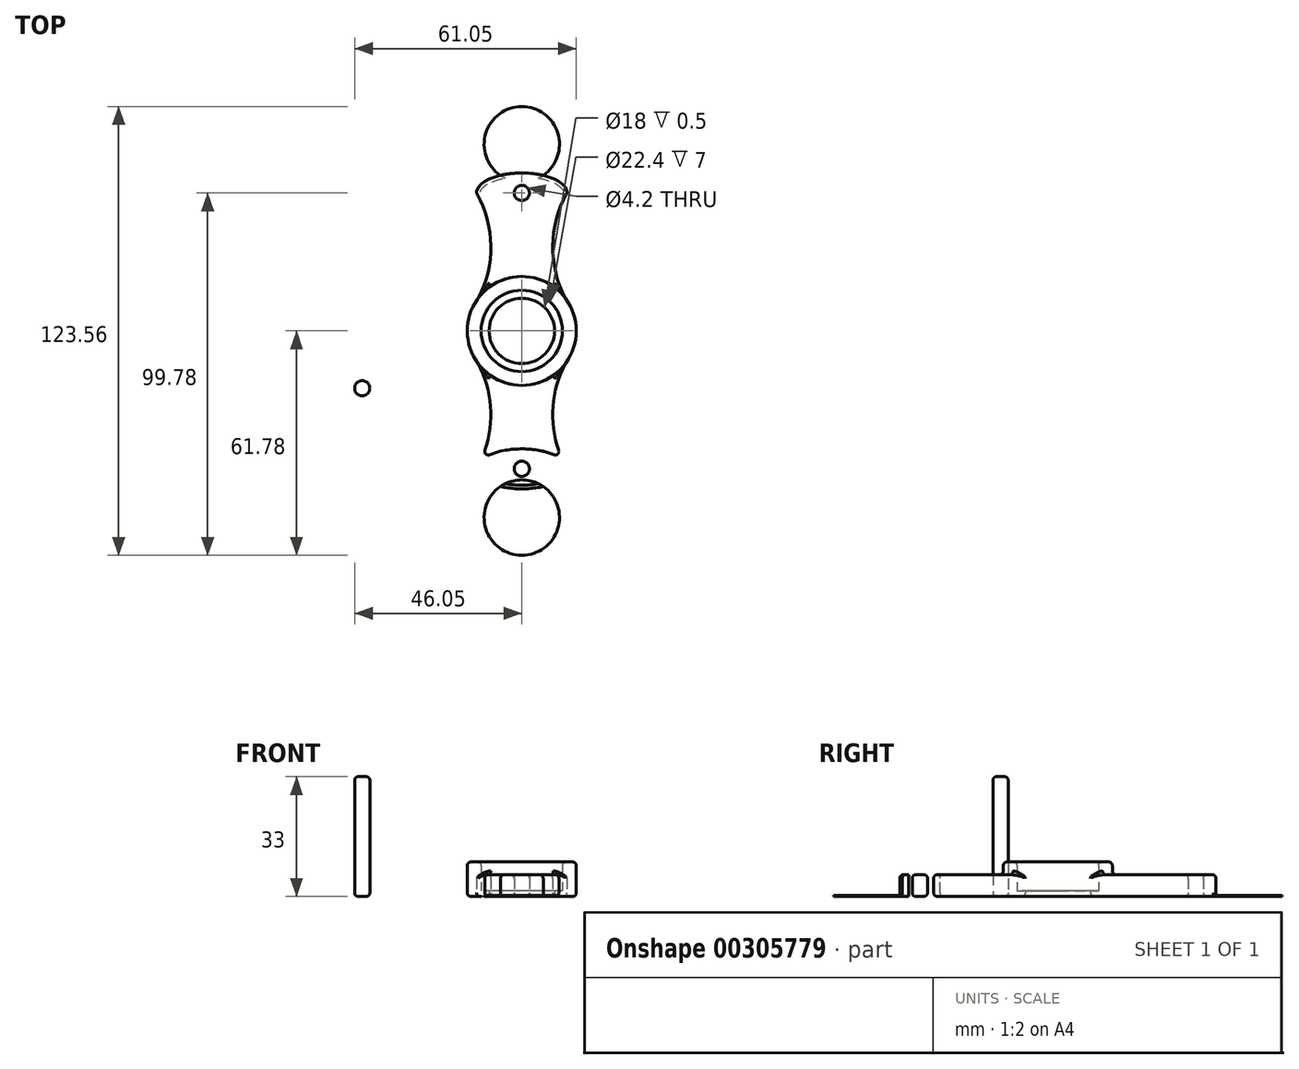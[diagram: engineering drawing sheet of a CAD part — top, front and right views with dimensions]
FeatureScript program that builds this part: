
annotation { "Feature Type Name" : "Feature", "Feature Type Description" : "" }
export const myFeature = defineFeature(function(context is Context, id is Id, definition is map)
    precondition{}
    {
        {
            var Q0;
            Q0=qCreatedBy(makeId("Top.planeOp"),FACE);
            var sketch = newSketch(context, id + "F0", { "sketchPlane" : qUnion([Q0])});
            skCircle(sketch, "E0", {"center": v(0, 38) * mm, "radius": 2.1 * mm});
            skCircle(sketch, "E1", {"center": v(0, 0) * mm, "radius": 9 * mm});
            skCircle(sketch, "E2", {"center": v(0, 0) * mm, "radius": 11.2 * mm});
            skCircle(sketch, "E3", {"center": v(0, 0) * mm, "radius": 15 * mm});
            skArc(sketch, "E4.MirrorCS", {"start": v(-12, -9) * mm, "mid": v(-11.4, -10.22) * mm, "end": v(-10.83, -11.46) * mm});
            skCircle(sketch, "E5.MirrorC", {"center": v(0, -38) * mm, "radius": 2.1 * mm});
            skEllipse(sketch, "E6", {"center": v(0, -38) * mm, "majorRadius": 5.5 * mm, "minorRadius": 12.5 * mm, "majorAxis": v(0, -1)});
            skArc(sketch, "E7", {"start": v(-12.5, -38) * mm, "mid": v(-8.51, -23.56) * mm, "end": v(-12, -9) * mm});
            skPoint(sketch, "E8.MirrorCS.start.orphan", {"position": v(12, -9) * mm});
            skArc(sketch, "E9.MirrorCS", {"start": v(12.5, -38) * mm, "mid": v(8.51, -23.56) * mm, "end": v(12, -9) * mm});
            skPoint(sketch, "E10.orphan", {"position": v(-12.5, -38) * mm});
            skPoint(sketch, "E11.orphan", {"position": v(12.5, -38) * mm});
            skArc(sketch, "E12.MirrorCS", {"start": v(-12.5, 38) * mm, "mid": v(-8.51, 23.56) * mm, "end": v(-12, 9) * mm});
            skArc(sketch, "E13.MirrorCS", {"start": v(12.5, 38) * mm, "mid": v(8.51, 23.56) * mm, "end": v(12, 9) * mm});
            skEllipse(sketch, "E14.MirrorC", {"center": v(0, 38) * mm, "majorRadius": 5.5 * mm, "minorRadius": 12.5 * mm, "majorAxis": v(0, 1)});
            skCircle(sketch, "E15.MirrorC", {"center": v(-31.5, -36.18) * mm, "radius": 2.1 * mm});
            skEllipse(sketch, "E16", {"center": v(-31.5, -36.18) * mm, "majorRadius": 5.5 * mm, "minorRadius": 12.5 * mm, "majorAxis": v(0, -1)});
            skCircle(sketch, "E17.MirrorC", {"center": v(-43.95, -15.8) * mm, "radius": 2.1 * mm});
            skEllipticalArc(sketch, "E18", {});
            skCircle(sketch, "E19", {"center": v(0, -51.4) * mm, "radius": 10.38 * mm});
            skCircle(sketch, "E20.MirrorC", {"center": v(0, 51.4) * mm, "radius": 10.38 * mm});
            skArc(sketch, "E21", {"start": v(-55.22, -13.41) * mm, "mid": v(-53.63, -9.12) * mm, "end": v(-52.7, -4.64) * mm});
            skArc(sketch, "E22.MirrorCS", {"start": v(-32.68, -13.41) * mm, "mid": v(-34.28, -9.12) * mm, "end": v(-35.2, -4.64) * mm});
            skPoint(sketch, "E23.orphan", {"position": v(-56.45, -15.8) * mm});
            skArc(sketch, "E24", {"start": v(-39.27, -0.36) * mm, "mid": v(-43.95, 0.06) * mm, "end": v(-48.64, -0.36) * mm});
            skPoint(sketch, "E25.visualSharp", {"position": v(-52.47, -1.36) * mm});
            skArc(sketch, "E25.filletArc", {"start": v(-48.64, -0.36) * mm, "mid": v(-51.37, -1.83) * mm, "end": v(-52.7, -4.64) * mm});
            skPoint(sketch, "E26.visualSharp", {"position": v(-35.44, -1.36) * mm});
            skArc(sketch, "E26.filletArc", {"start": v(-35.2, -4.64) * mm, "mid": v(-36.54, -1.83) * mm, "end": v(-39.27, -0.36) * mm});
            const initialGuessF0  = {"E18": [-0.04395357987462184, -0.015792207916784852, 0, -1, 0.0055, 0.0125, 4.265086725092129, 2.0180985820874437]};
            skSetInitialGuess(sketch, initialGuessF0);
            skSolve(sketch);
        }
        {
            var Q0;
            Q0=makeQuery(id+"F0.imprint","IMPRINT",FACE,{"disambiguationData":[TD([[makeQuery(id+"F0.imprint","IMPRINT",EDGE,{"derivedFrom":sQuery(id+"F0.wireOp",EDGE,"E1")}),-1.0]])]});
            extrude(context, id + "F1", {"entities" : qUnion([Q0]), "depth" : 1.5 * mm});
        }
        {
            var Q0;
            Q0=makeQuery(id+"F0.imprint","IMPRINT",FACE,{"disambiguationData":[TD([[makeQuery(id+"F0.imprint","IMPRINT",EDGE,{"derivedFrom":sQuery(id+"F0.wireOp",EDGE,"E2")}),-1.0]])]});
            extrude(context, id + "F2", {"entities" : qUnion([Q0]), "operationType" : NewBodyOperationType.ADD, "depth" : 9.5 * mm});
        }
        {
            var Q0;
            {var subQ0=sQuery(id+"F0.wireOp",EDGE,"E12.MirrorCS");var subQ1=sQuery(id+"F0.wireOp",EDGE,"E3");var subQ2=makeQuery(id+"F0.imprint","INTERSECT",VERTEX,{"derivedFrom":[subQ1,subQ0]});Q0=makeQuery(id+"F0.imprint","IMPRINT",FACE,{"disambiguationData":[TD([[makeQuery(id+"F0.imprint","IMPRINT",EDGE,{"disambiguationData":[TD([[subQ2,1.0]])],"derivedFrom":subQ1}),-1.0]])]});}
            var Q1;
            Q1=makeQuery(id+"F0.imprint","IMPRINT",FACE,{"disambiguationData":[TD([[makeQuery(id+"F0.imprint","IMPRINT",EDGE,{"derivedFrom":sQuery(id+"F0.wireOp",EDGE,"E0")}),-1.0]])]});
            var Q2;
            {var subQ3=sQuery(id+"F0.wireOp",EDGE,"E6");var subQ7=sQuery(id+"F0.wireOp",EDGE,"E9.MirrorCS");var subQ8=makeQuery(id+"F0.imprint","INTERSECT",VERTEX,{"disambiguationData":[OD(1.0)],"derivedFrom":[subQ3,subQ7]});Q2=makeQuery(id+"F0.imprint","IMPRINT",FACE,{"disambiguationData":[TD([[makeQuery(id+"F0.imprint","IMPRINT",EDGE,{"disambiguationData":[TD([[subQ8,-1.0]])],"derivedFrom":subQ3}),-1.0]])]});}
            var Q3;
            Q3=makeQuery(id+"F0.imprint","IMPRINT",FACE,{"disambiguationData":[TD([[makeQuery(id+"F0.imprint","IMPRINT",EDGE,{"derivedFrom":sQuery(id+"F0.wireOp",EDGE,"E5.MirrorC")}),1.0]])]});
            var Q4;
            {var subQ0=sQuery(id+"F0.wireOp",EDGE,"E20.MirrorC");var subQ1=sQuery(id+"F0.wireOp",EDGE,"E14.MirrorC");var subQ2=makeQuery(id+"F0.imprint","INTERSECT",VERTEX,{"disambiguationData":[OD(0.0)],"derivedFrom":[subQ1,subQ0]});Q4=makeQuery(id+"F0.imprint","IMPRINT",FACE,{"disambiguationData":[TD([[makeQuery(id+"F0.imprint","IMPRINT",EDGE,{"disambiguationData":[TD([[subQ2,-1.0]])],"derivedFrom":subQ1}),1.0]])]});}
            var Q5;
            {var subQ0=sQuery(id+"F0.wireOp",EDGE,"E19");var subQ1=sQuery(id+"F0.wireOp",EDGE,"E6");var subQ2=makeQuery(id+"F0.imprint","INTERSECT",VERTEX,{"disambiguationData":[OD(0.0)],"derivedFrom":[subQ1,subQ0]});Q5=makeQuery(id+"F0.imprint","IMPRINT",FACE,{"disambiguationData":[TD([[makeQuery(id+"F0.imprint","IMPRINT",EDGE,{"disambiguationData":[TD([[subQ2,-1.0]])],"derivedFrom":subQ1}),1.0]])]});}
            extrude(context, id + "F3", {"entities" : qUnion([Q0, Q1, Q2, Q3, Q4, Q5]), "operationType" : NewBodyOperationType.ADD, "depth" : 6 * mm});
        }
        {
            var Q0;
            Q0=makeQuery(id+"F0.imprint","IMPRINT",FACE,{"disambiguationData":[TD([[makeQuery(id+"F0.imprint","IMPRINT",EDGE,{"derivedFrom":sQuery(id+"F0.wireOp",EDGE,"E17.MirrorC")}),1.0]])]});
            var Q1;
            Q1=makeQuery(id+"F0.imprint","IMPRINT",FACE,{"disambiguationData":[TD([[makeQuery(id+"F0.imprint","IMPRINT",EDGE,{"derivedFrom":sQuery(id+"F0.wireOp",EDGE,"E15.MirrorC")}),1.0]])]});
            extrude(context, id + "F4", {"entities" : qUnion([Q0, Q1]), "depth" : 33 * mm});
        }
        {
            var Q0;
            Q0=makeQuery(id+"F4.opExtrude","CAP_FACE",FACE,{"disambiguationData":[OSD([sQuery(id+"F0.wireOp",EDGE,"E17.MirrorC"),sQuery(id+"F0.wireOp",EDGE,"E18")])],"isStart":true});
            var Q1;
            Q1=makeQuery(id+"F4.opExtrude","CAP_EDGE",EDGE,{"disambiguationData":[OSD([sQuery(id+"F0.wireOp",EDGE,"E18")])],"isStart":false});
            var Q2;
            Q2=makeQuery(id+"F4.opExtrude","CAP_FACE",FACE,{"disambiguationData":[OSD([sQuery(id+"F0.wireOp",EDGE,"E17.MirrorC"),sQuery(id+"F0.wireOp",EDGE,"E18")])],"isStart":false});
            var Q3;
            Q3=makeQuery(id+"F4.opExtrude","SWEPT_FACE",FACE,{"disambiguationData":[OSD([sQuery(id+"F0.wireOp",EDGE,"E18")])]});
            var Q4;
            Q4=makeQuery(id+"F4.opExtrude","SWEPT_FACE",FACE,{"disambiguationData":[OSD([sQuery(id+"F0.wireOp",EDGE,"E17.MirrorC")])]});
            var Q5;
            Q5=makeQuery(id+"F4.opExtrude","SWEPT_FACE",FACE,{"disambiguationData":[OSD([sQuery(id+"F0.wireOp",EDGE,"E16")])]});
            var Q6;
            Q6=makeQuery(id+"F4.opExtrude","CAP_EDGE",EDGE,{"disambiguationData":[OSD([sQuery(id+"F0.wireOp",EDGE,"E16")])],"isStart":false});
            var Q7;
            Q7=makeQuery(id+"F4.opExtrude","CAP_FACE",FACE,{"disambiguationData":[OSD([sQuery(id+"F0.wireOp",EDGE,"E15.MirrorC"),sQuery(id+"F0.wireOp",EDGE,"E16")])],"isStart":false});
            var Q8;
            Q8=makeQuery(id+"F4.opExtrude","CAP_FACE",FACE,{"disambiguationData":[OSD([sQuery(id+"F0.wireOp",EDGE,"E15.MirrorC"),sQuery(id+"F0.wireOp",EDGE,"E16")])],"isStart":true});
            var Q9;
            Q9=makeQuery(id+"F4.opExtrude","SWEPT_FACE",FACE,{"disambiguationData":[OSD([sQuery(id+"F0.wireOp",EDGE,"E15.MirrorC")])]});
            var Q10;
            Q10=makeQuery(id+"F4.opExtrude","CAP_EDGE",EDGE,{"disambiguationData":[OSD([sQuery(id+"F0.wireOp",EDGE,"E18")])],"isStart":true});
            var Q11;
            Q11=makeQuery(id+"F4.opExtrude","CAP_EDGE",EDGE,{"disambiguationData":[OSD([sQuery(id+"F0.wireOp",EDGE,"E17.MirrorC")])],"isStart":false});
            var Q12;
            Q12=makeQuery(id+"F4.opExtrude","CAP_EDGE",EDGE,{"disambiguationData":[OSD([sQuery(id+"F0.wireOp",EDGE,"E17.MirrorC")])],"isStart":true});
            var Q13;
            Q13=makeQuery(id+"F4.opExtrude","CAP_EDGE",EDGE,{"disambiguationData":[OSD([sQuery(id+"F0.wireOp",EDGE,"E16")])],"isStart":true});
            var Q14;
            Q14=makeQuery(id+"F4.opExtrude","CAP_EDGE",EDGE,{"disambiguationData":[OSD([sQuery(id+"F0.wireOp",EDGE,"E15.MirrorC")])],"isStart":false});
            var Q15;
            Q15=makeQuery(id+"F4.opExtrude","CAP_EDGE",EDGE,{"disambiguationData":[OSD([sQuery(id+"F0.wireOp",EDGE,"E15.MirrorC")])],"isStart":true});
            fillet(context, id + "F5", {"entities" : qUnion([Q0, Q1, Q2, Q3, Q4, Q5, Q6, Q7, Q8, Q9, Q10, Q11, Q12, Q13, Q14, Q15]), "radius" : 1 * mm, "tangentPropagation" : true, "allowEdgeOverflow" : false});
        }
        {
            var Q0;
            {var subQ0=sQuery(id+"F0.wireOp",EDGE,"E19");var subQ1=sQuery(id+"F0.wireOp",EDGE,"E6");var subQ2=makeQuery(id+"F0.imprint","INTERSECT",VERTEX,{"disambiguationData":[OD(0.0)],"derivedFrom":[subQ1,subQ0]});Q0=makeQuery(id+"F0.imprint","IMPRINT",FACE,{"disambiguationData":[TD([[makeQuery(id+"F0.imprint","IMPRINT",EDGE,{"disambiguationData":[TD([[subQ2,-1.0]])],"derivedFrom":subQ1}),-1.0]])]});}
            var Q1;
            {var subQ0=sQuery(id+"F0.wireOp",EDGE,"E20.MirrorC");var subQ1=sQuery(id+"F0.wireOp",EDGE,"E14.MirrorC");var subQ2=makeQuery(id+"F0.imprint","INTERSECT",VERTEX,{"disambiguationData":[OD(0.0)],"derivedFrom":[subQ1,subQ0]});Q1=makeQuery(id+"F0.imprint","IMPRINT",FACE,{"disambiguationData":[TD([[makeQuery(id+"F0.imprint","IMPRINT",EDGE,{"disambiguationData":[TD([[subQ2,-1.0]])],"derivedFrom":subQ1}),-1.0]])]});}
            extrude(context, id + "F6", {"entities" : qUnion([Q0, Q1]), "operationType" : NewBodyOperationType.ADD, "depth" : 0.3 * mm});
        }
        {
            var Q0;
            Q0=makeQuery(id+"F3.opExtrude","SWEPT_FACE",FACE,{"disambiguationData":[OSD([sQuery(id+"F0.wireOp",EDGE,"E7")])]});
            var Q1;
            Q1=makeQuery(id+"F3.opExtrude","SWEPT_FACE",FACE,{"disambiguationData":[OSD([sQuery(id+"F0.wireOp",EDGE,"E12.MirrorCS")])]});
            var Q2;
            Q2=makeQuery(id+"F2.opExtrude","SWEPT_FACE",FACE,{"disambiguationData":[OSD([sQuery(id+"F0.wireOp",EDGE,"E3")])]});
            var Q3;
            Q3=makeQuery(id+"F3.opExtrude","SWEPT_FACE",FACE,{"disambiguationData":[OSD([sQuery(id+"F0.wireOp",EDGE,"E13.MirrorCS")])]});
            var Q4;
            Q4=makeQuery(id+"F3.opExtrude","SWEPT_FACE",FACE,{"disambiguationData":[OSD([sQuery(id+"F0.wireOp",EDGE,"E9.MirrorCS")])]});
            var Q5;
            Q5=makeQuery(id+"F3.opExtrude","CAP_EDGE",EDGE,{"disambiguationData":[OSD([sQuery(id+"F0.wireOp",EDGE,"E14.MirrorC")])],"isStart":false});
            var Q6;
            {var subQ2=sQuery(id+"F0.wireOp",EDGE,"E14.MirrorC");var subQ3=sQuery(id+"F0.wireOp",EDGE,"E12.MirrorCS");Q6=makeQuery(id+"F6.boolean.opBoolean","SPLIT",EDGE,{"disambiguationData":[TD([makeQuery(id+"F3.opExtrude","SWEPT_FACE",FACE,{"disambiguationData":[OSD([subQ3])]})])],"derivedFrom":makeQuery(id+"F3.opExtrude","CAP_EDGE",EDGE,{"disambiguationData":[OSD([subQ2])],"isStart":true})});}
            var Q7;
            {var subQ2=sQuery(id+"F0.wireOp",EDGE,"E14.MirrorC");var subQ3=sQuery(id+"F0.wireOp",EDGE,"E13.MirrorCS");Q7=makeQuery(id+"F6.boolean.opBoolean","SPLIT",EDGE,{"disambiguationData":[TD([makeQuery(id+"F3.opExtrude","SWEPT_FACE",FACE,{"disambiguationData":[OSD([subQ3])]})])],"derivedFrom":makeQuery(id+"F3.opExtrude","CAP_EDGE",EDGE,{"disambiguationData":[OSD([subQ2])],"isStart":true})});}
            var Q8;
            Q8=makeQuery(id+"F2.opExtrude","CAP_EDGE",EDGE,{"disambiguationData":[OSD([sQuery(id+"F0.wireOp",EDGE,"E2")])],"isStart":false});
            var Q9;
            Q9=makeQuery(id+"F3.opExtrude","CAP_EDGE",EDGE,{"disambiguationData":[OSD([sQuery(id+"F0.wireOp",EDGE,"E6")])],"isStart":false});
            var Q10;
            {var subQ0=sQuery(id+"F0.wireOp",EDGE,"E7");var subQ1=sQuery(id+"F0.wireOp",EDGE,"E6");Q10=makeQuery(id+"F6.boolean.opBoolean","SPLIT",EDGE,{"disambiguationData":[TD([makeQuery(id+"F3.opExtrude","SWEPT_FACE",FACE,{"disambiguationData":[OSD([subQ0])]})])],"derivedFrom":makeQuery(id+"F3.opExtrude","CAP_EDGE",EDGE,{"disambiguationData":[OSD([subQ1])],"isStart":true})});}
            var Q11;
            {var subQ0=sQuery(id+"F0.wireOp",EDGE,"E9.MirrorCS");var subQ1=sQuery(id+"F0.wireOp",EDGE,"E6");Q11=makeQuery(id+"F6.boolean.opBoolean","SPLIT",EDGE,{"disambiguationData":[TD([makeQuery(id+"F3.opExtrude","SWEPT_FACE",FACE,{"disambiguationData":[OSD([subQ0])]})])],"derivedFrom":makeQuery(id+"F3.opExtrude","CAP_EDGE",EDGE,{"disambiguationData":[OSD([subQ1])],"isStart":true})});}
            var Q12;
            Q12=makeQuery(id+"F3.opExtrude","SWEPT_FACE",FACE,{"disambiguationData":[OSD([sQuery(id+"F0.wireOp",EDGE,"E5.MirrorC")])]});
            var Q13;
            Q13=makeQuery(id+"F3.opExtrude","SWEPT_FACE",FACE,{"disambiguationData":[OSD([sQuery(id+"F0.wireOp",EDGE,"E0")])]});
            var Q14;
            Q14=makeQuery(id+"F1.opExtrude","CAP_EDGE",EDGE,{"disambiguationData":[OSD([sQuery(id+"F0.wireOp",EDGE,"E1")])],"isStart":true});
            fillet(context, id + "F7", {"entities" : qUnion([Q0, Q1, Q2, Q3, Q4, Q5, Q6, Q7, Q8, Q9, Q10, Q11, Q12, Q13, Q14]), "radius" : 1 * mm, "tangentPropagation" : true, "allowEdgeOverflow" : false});
        }
        {
            var Q0;
            Q0=makeQuery(id+"F4.opExtrude","SWEPT_BODY",BODY,{"disambiguationData":[OSD([sQuery(id+"F0.wireOp",EDGE,"E15.MirrorC"),sQuery(id+"F0.wireOp",EDGE,"E16")])]});
            deleteBodies(context, id + "F8", {"entities" : qUnion([Q0])});
        }
    });
